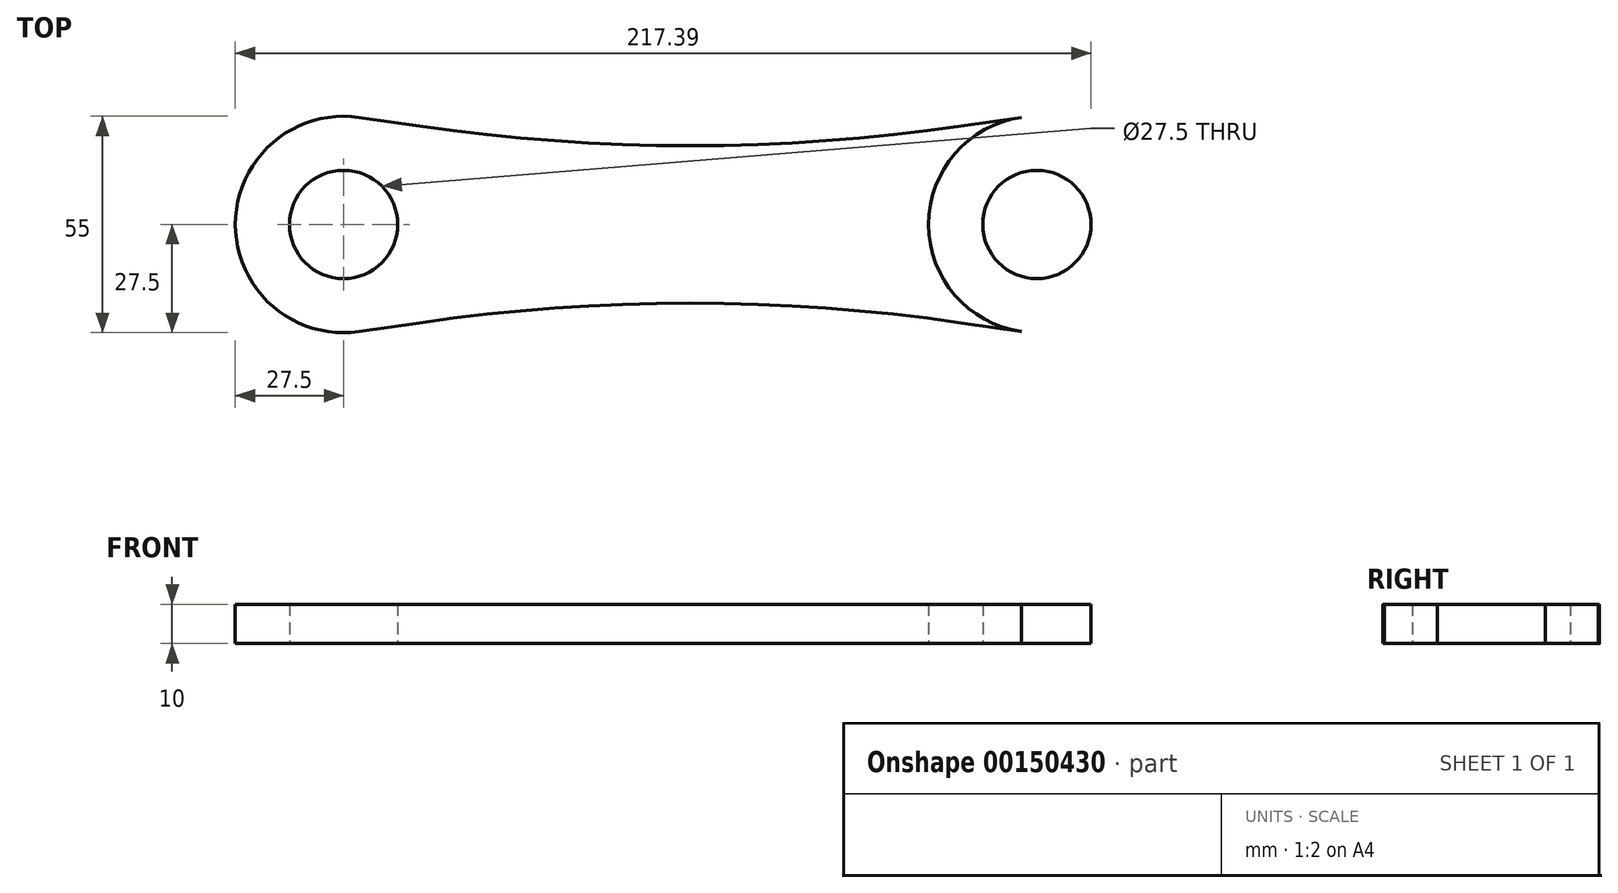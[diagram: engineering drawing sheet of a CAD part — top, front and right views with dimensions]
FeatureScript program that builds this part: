
annotation { "Feature Type Name" : "Feature", "Feature Type Description" : "" }
export const myFeature = defineFeature(function(context is Context, id is Id, definition is map)
    precondition{}
    {
        {
            var Q0;
            Q0=qCreatedBy(makeId("Top.planeOp"),FACE);
            var sketch = newSketch(context, id + "F0", { "sketchPlane" : qUnion([Q0])});
            skCircle(sketch, "E0", {"center": v(-88.07, 0) * mm, "radius": 27.5 * mm});
            skCircle(sketch, "E1", {"center": v(-88.07, 0) * mm, "radius": 13.75 * mm});
            skLineSegment(sketch, "E2", {"start": v(-84.12, 27.21) * mm, "end": v(0, 15) * mm});
            skLineSegment(sketch, "E3.MirrorCS", {"start": v(-84.12, -27.21) * mm, "end": v(0, -15) * mm});
            skLineSegment(sketch, "E4.MirrorCS", {"start": v(84.12, 27.21) * mm, "end": v(0, 15) * mm});
            skLineSegment(sketch, "E5.MirrorCS", {"start": v(84.12, -27.21) * mm, "end": v(0, -15) * mm});
            skCircle(sketch, "E6.MirrorC", {"center": v(88.07, 0) * mm, "radius": 13.75 * mm});
            skCircle(sketch, "E7.MirrorC", {"center": v(88.07, 0) * mm, "radius": 27.5 * mm});
            skSolve(sketch);
        }
        {
            var Q0;
            {var subQ2=sQuery(id+"F0.wireOp",EDGE,"E2");Q0=makeQuery(id+"F0.imprint","IMPRINT",FACE,{"disambiguationData":[TD([[makeQuery(id+"F0.imprint","IMPRINT",EDGE,{"derivedFrom":subQ2}),-1.0]])]});}
            var Q1;
            Q1=makeQuery(id+"F0.imprint","IMPRINT",FACE,{"disambiguationData":[TD([[makeQuery(id+"F0.imprint","IMPRINT",EDGE,{"derivedFrom":sQuery(id+"F0.wireOp",EDGE,"E1")}),-1.0]])]});
            var Q2;
            Q2=makeQuery(id+"F0.imprint","IMPRINT",FACE,{"disambiguationData":[TD([[makeQuery(id+"F0.imprint","IMPRINT",EDGE,{"derivedFrom":sQuery(id+"F0.wireOp",EDGE,"E6.MirrorC")}),1.0]])]});
            extrude(context, id + "F1", {"entities" : qUnion([Q0, Q1, Q2]), "depth" : 10 * mm});
        }
        {
            var Q0;
            Q0=makeQuery(id+"F1.opExtrude","SWEPT_EDGE",EDGE,{"disambiguationData":[OSD([sQuery(id+"F0.wireOp",EDGE,"E3.MirrorCS"),sQuery(id+"F0.wireOp",EDGE,"E5.MirrorCS")])]});
            var Q1;
            Q1=makeQuery(id+"F1.opExtrude","SWEPT_EDGE",EDGE,{"disambiguationData":[OSD([sQuery(id+"F0.wireOp",EDGE,"E2"),sQuery(id+"F0.wireOp",EDGE,"E4.MirrorCS")])]});
            fillet(context, id + "F2", {"entities" : qUnion([Q0, Q1]), "radius" : 478.62 * mm, "tangentPropagation" : true, "allowEdgeOverflow" : false});
        }
    });
